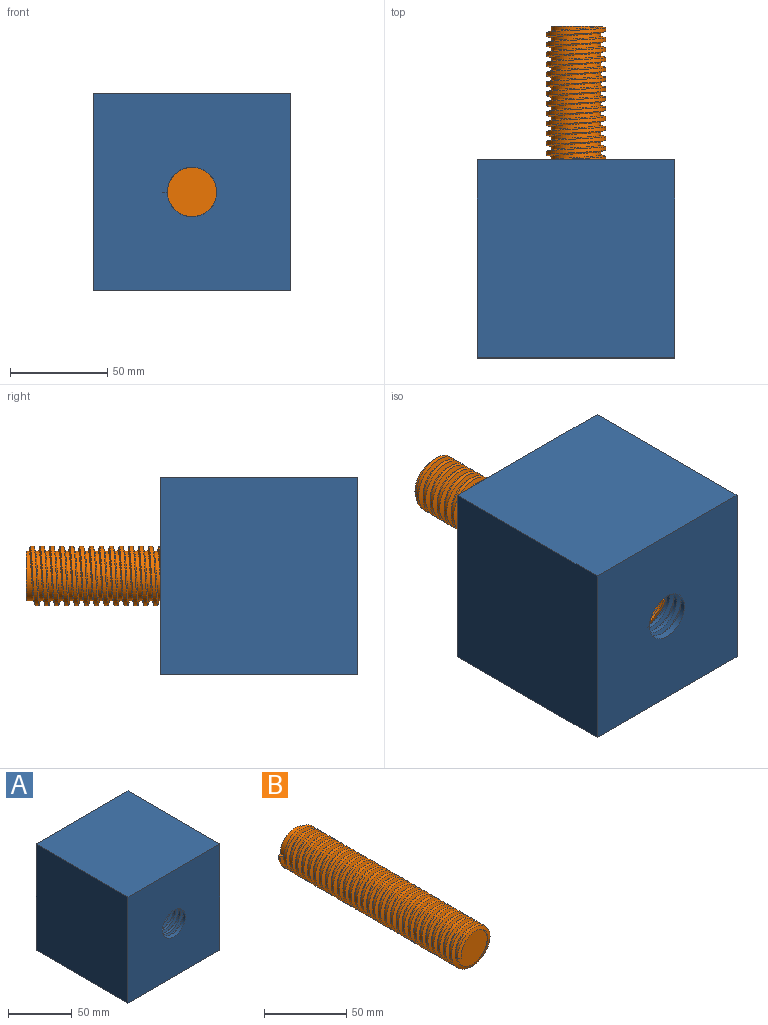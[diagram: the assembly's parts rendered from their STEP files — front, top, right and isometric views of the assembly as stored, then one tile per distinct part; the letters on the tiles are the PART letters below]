
ASSEMBLY  parts=2 mates=1
PART A: 11 faces, bbox 101.6x103.1x101.6 mm
  f0: plane 101.6x101.6mm, normal (1,0,0), area 10322.6mm2, adj f1,f4,f5,f6
  f1: plane 101.6x101.6mm, normal (0,0,1), area 10322.6mm2, adj f0,f2,f5,f6
  f2: plane 101.6x101.6mm, normal (-1,0,0), area 10322.6mm2, adj f1,f4,f5,f6
  f3: cylinder r=12.7mm len=101.6mm, axis (0,1,0), area 4383.8mm2, adj f5,f6,f7,f9,f10
  f4: plane 101.6x101.6mm, normal (0,0,-1), area 10322.6mm2, adj f0,f2,f5,f6
  f5: plane 101.6x101.6mm, normal (0,-1,0), area 9815.9mm2, adj f0,f1,f2,f3,f4
  f6: plane 101.6x101.6mm, normal (0,1,0), area 9705.2mm2, adj f0,f1,f2,f3,f4,f7,f8,f9
  f7: bspline ~102.26x35.2mm, area 4622.8mm2, adj f3,f6,f8,f10
  f8: cylinder r=15.24mm len=100.94mm, axis (0,-1,0), area 2710.3mm2, adj f6,f7,f9,f10
  f9: bspline ~100.56x35.2mm, area 4478mm2, adj f3,f6,f8,f10
  f10: plane 3.2x2.54mm, normal (0,0,1), area 6.5mm2, adj f3,f7,f8,f9
PART B: 9 faces, bbox 30.5x155.6x35.2 mm
  f0: cylinder r=12.7mm len=152.4mm, axis (0,1,0), area 5568.7mm2, adj f1,f2,f4,f6,f8
  f1: plane 25.4x25.4mm, normal (0,-1,0), area 506.7mm2, adj f0,f3
  f2: plane 25.4x25.4mm, normal (0,1,0), area 506.7mm2, adj f0
  f3: cylinder r=12.7mm len=25.4mm, axis (0,-1,0), area 80.3mm2, adj f1,f5,f6
  f4: plane 3.2x2.54mm, normal (0,0,1), area 6.5mm2, adj f0,f6,f7,f8
  f5: plane 3.2x2.54mm, normal (0,0,-1), area 6.5mm2, adj f3,f6,f7,f8
  f6: bspline ~153.06x35.2mm, area 6902.2mm2, adj f0,f3,f4,f5,f7
  f7: cylinder r=15.24mm len=154.28mm, axis (0,-1,0), area 5409.6mm2, adj f4,f5,f6,f8
  f8: bspline ~153.06x35.2mm, area 6902.2mm2, adj f0,f4,f5,f7
PLACE A t=(10.18,92.51,18.78)mm fixed
PLACE B rot(axis=(0,-1,0),163.9deg) t=(-40.62,85.12,69.58)mm
MATE cylindrical A.f3 <-> B.f0  axis (0,1,0) through (-40.62,92.51,69.58)mm
